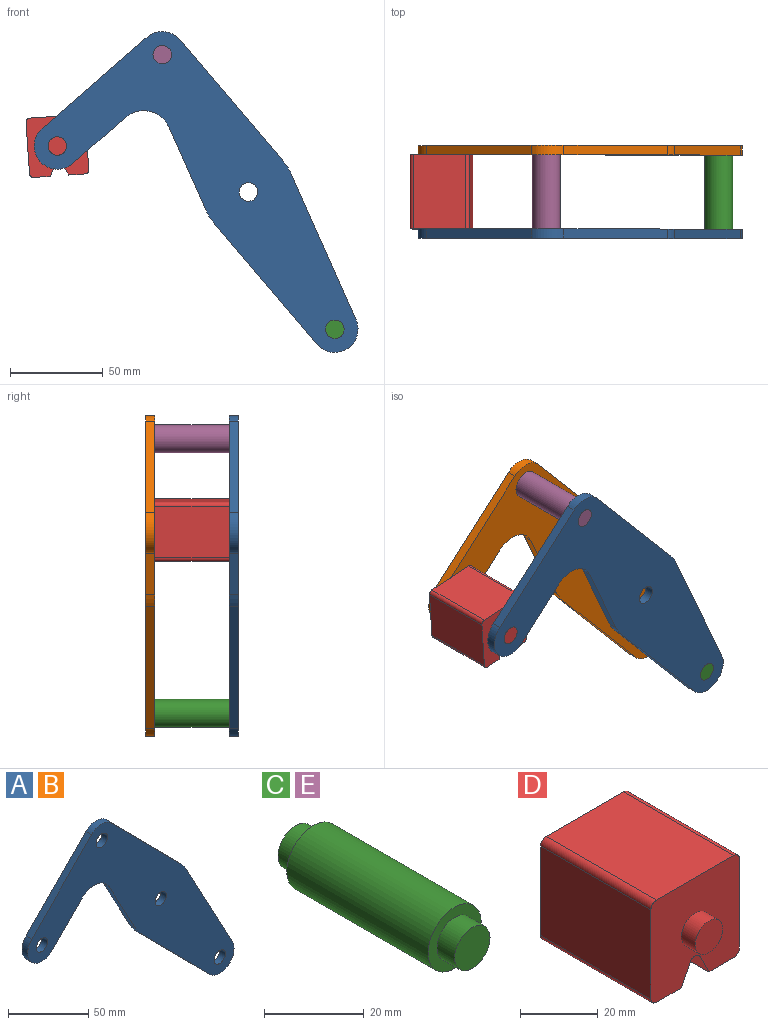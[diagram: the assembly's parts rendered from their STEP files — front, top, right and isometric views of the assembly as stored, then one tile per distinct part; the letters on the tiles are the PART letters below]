
ASSEMBLY  parts=5 mates=3
PART A: 18 faces, bbox 181.7x5x165.8 mm
  f0: plane 43.49x23.35mm, normal (-0.88,0,-0.47), area 246.8mm2, adj f1,f14,f16,f17
  f1: cylinder r=25mm len=5.75mm, axis (0,1,0), area 35.8mm2, adj f0,f2,f16,f17
  f2: plane 61.6x60.87mm, normal (-0.71,0,-0.7), area 433mm2, adj f1,f3,f16,f17
  f3: cylinder r=12.5mm len=21.39mm, axis (0,1,0), area 178.4mm2, adj f2,f4,f16,f17
  f4: plane 76.3x40.96mm, normal (0.88,0,0.47), area 433mm2, adj f3,f5,f16,f17
  f5: cylinder r=25mm len=5.75mm, axis (0,1,0), area 35.8mm2, adj f4,f6,f16,f17
  f6: plane 61.6x60.87mm, normal (0.71,0,0.7), area 433mm2, adj f5,f7,f16,f17
  f7: cylinder r=12.5mm len=17.78mm, axis (0,1,0), area 98.9mm2, adj f6,f8,f16,f17
  f8: plane 53.35x52.71mm, normal (-0.71,0,0.7), area 375mm2, adj f7,f9,f16,f17
  f9: cylinder r=12.5mm len=21.39mm, axis (0,1,0), area 196.3mm2, adj f8,f10,f16,f17
  f10: plane 26.86x26.54mm, normal (0.71,0,-0.7), area 188.8mm2, adj f9,f14,f16,f17
  f11: cylinder r=5mm len=10mm, axis (0,1,0), area 157.1mm2, adj f16,f17
  f12: cylinder r=5mm len=10mm, axis (0,1,0), area 157.1mm2, adj f16,f17
  f13: cylinder r=5mm len=10mm, axis (0,1,0), area 157.1mm2, adj f16,f17
  f14: cylinder r=15mm len=23.89mm, axis (0,1,0), area 140.2mm2, adj f0,f10,f16,f17
  f15: cylinder r=5mm len=10mm, axis (0,1,0), area 157.1mm2, adj f16,f17
  f16: plane 181.66x165.78mm, normal (0,-1,0), area 8710.1mm2, adj f0,f1,f2,f3,f4,f5,f6,f7
  f17: plane 181.66x165.78mm, normal (0,1,0), area 8710.1mm2, adj f0,f1,f2,f3,f4,f5,f6,f7
PART B: same geometry as A
PART C: 7 faces, bbox 15x50x15 mm
  f0: cylinder r=7.5mm len=40mm, axis (0,-1,0), area 1885mm2, adj f2,f5
  f1: cylinder r=5mm len=10mm, axis (0,1,0), area 157.1mm2, adj f2,f3
  f2: plane 15x15mm, normal (0,-1,0), area 98.2mm2, adj f0,f1
  f3: plane 10x10mm, normal (0,-1,0), area 78.5mm2, adj f1
  f4: cylinder r=5mm len=10mm, axis (0,-1,0), area 157.1mm2, adj f5,f6
  f5: plane 15x15mm, normal (0,1,0), area 98.2mm2, adj f0,f4
  f6: plane 10x10mm, normal (0,1,0), area 78.5mm2, adj f4
PART D: 18 faces, bbox 32.1x50x32.1 mm
  f0: plane 40x28.08mm, normal (1,0,0), area 1123.1mm2, adj f4,f10,f13,f14
  f1: plane 40x9.04mm, normal (0,0,-1), area 361.6mm2, adj f2,f4,f10,f14
  f2: plane 40x6.42mm, normal (-0.89,0,-0.45), area 287.2mm2, adj f1,f4,f10,f15
  f3: plane 40x6.42mm, normal (0.89,0,-0.45), area 287.2mm2, adj f4,f5,f10,f15
  f4: plane 32.08x32.08mm, normal (0,-1,0), area 900.6mm2, adj f0,f1,f2,f3,f5,f6,f7,f9
  f5: plane 40x9.04mm, normal (0,0,-1), area 361.6mm2, adj f3,f4,f10,f16
  f6: plane 40x28.08mm, normal (0,0,1), area 1123.1mm2, adj f4,f10,f13,f17
  f7: plane 40x28.08mm, normal (-1,0,0), area 1123.1mm2, adj f4,f10,f16,f17
  f8: plane 10x10mm, normal (0,-1,0), area 78.5mm2, adj f9
  f9: cylinder r=5mm len=10mm, axis (0,1,0), area 157.1mm2, adj f4,f8
  f10: plane 32.08x32.08mm, normal (0,1,0), area 900.6mm2, adj f0,f1,f2,f3,f5,f6,f7,f12
  f11: plane 10x10mm, normal (0,1,0), area 78.5mm2, adj f12
  f12: cylinder r=5mm len=10mm, axis (0,-1,0), area 157.1mm2, adj f10,f11
  f13: cylinder r=2mm len=40mm, axis (0,1,0), area 125.7mm2, adj f0,f4,f6,f10
  f14: cylinder r=2mm len=40mm, axis (0,-1,0), area 125.7mm2, adj f0,f1,f4,f10
  f15: cylinder r=2mm len=40mm, axis (0,1,0), area 177.1mm2, adj f2,f3,f4,f10
  f16: cylinder r=2mm len=40mm, axis (0,1,0), area 125.7mm2, adj f4,f5,f7,f10
  f17: cylinder r=2mm len=40mm, axis (0,-1,0), area 125.7mm2, adj f4,f6,f7,f10
PART E: same geometry as C
PLACE A rot(axis=(0,1,0),4.3deg) t=(0,-20,0)mm fixed
PLACE B rot(axis=(0,1,0),4.3deg) t=(0,25,0)mm
PLACE C rot(axis=(0,1,0),4.3deg) t=(93.15,-20,-148.15)mm
PLACE D rot(axis=(0,-1,0),3.9deg) t=(2.47,-20,14.85)mm
PLACE E rot(axis=(0,1,0),4.3deg) t=(0,-20,0)mm
MATE fastened C.f0 <-> A.f3  axis (0,-1,0) through (46.57,-20,-74.08)mm
MATE revolute D.f9 <-> A.f9  axis (0,-1,0) through (-103.12,-20,24.81)mm
MATE fastened B.f7 <-> E.f0  axis (0,-1,0) through (-46.57,20,74.08)mm
